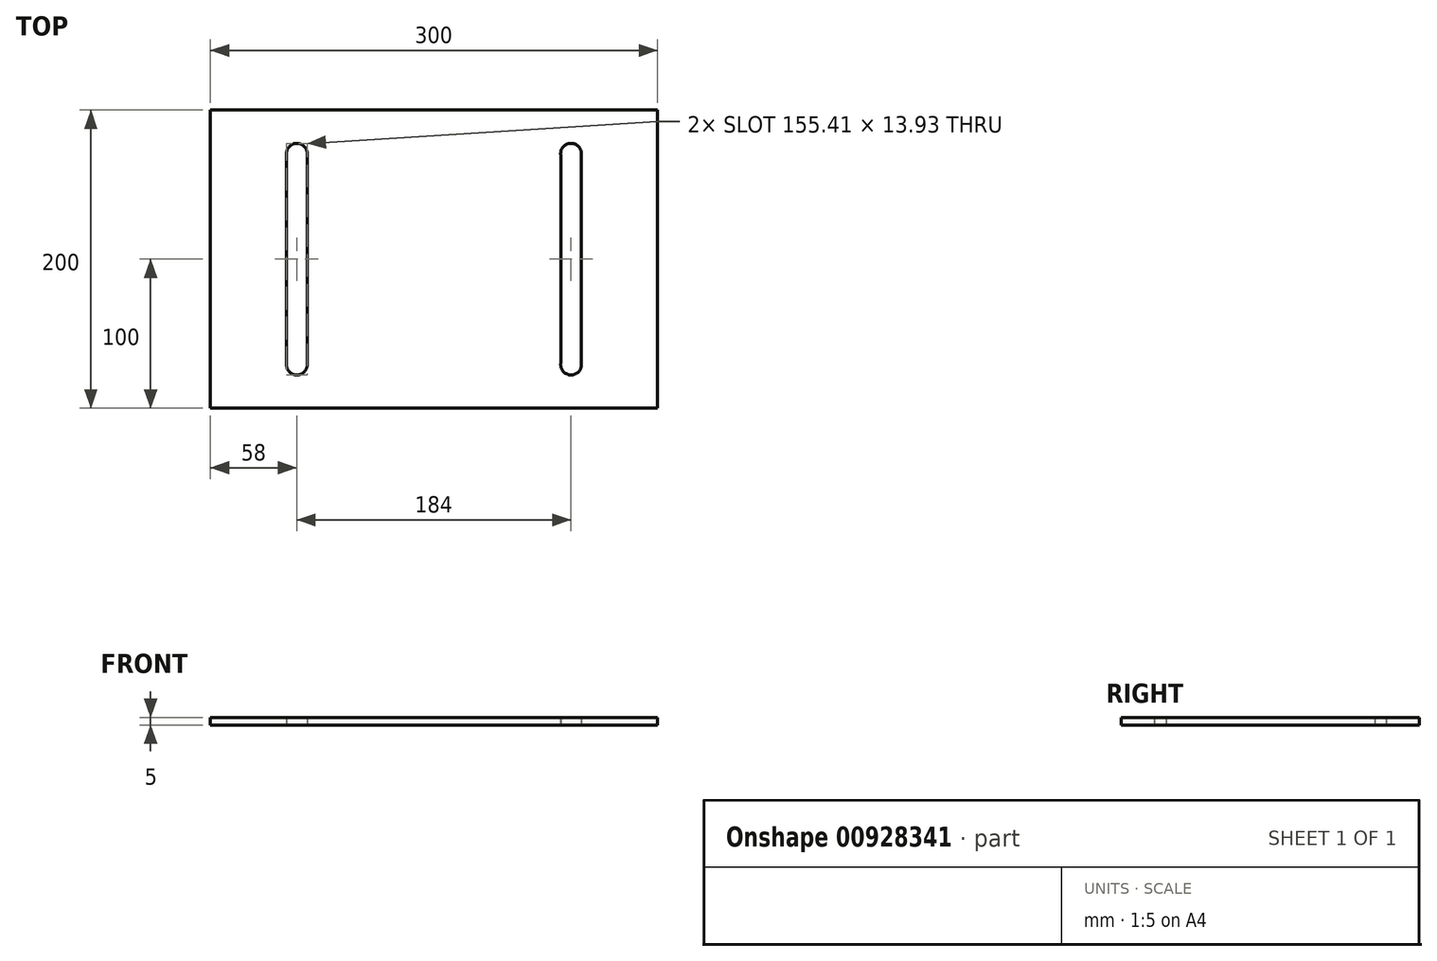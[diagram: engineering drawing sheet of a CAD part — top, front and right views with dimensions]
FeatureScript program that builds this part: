
annotation { "Feature Type Name" : "Feature", "Feature Type Description" : "" }
export const myFeature = defineFeature(function(context is Context, id is Id, definition is map)
    precondition{}
    {
        {
            var Q0;
            Q0=qCreatedBy(makeId("Top.planeOp"),FACE);
            var sketch = newSketch(context, id + "F0", { "sketchPlane" : qUnion([Q0])});
            skLineSegment(sketch, "E0.bottom", {"start": v(150, 100) * mm, "end": v(-150, 100) * mm});
            skLineSegment(sketch, "E0.top", {"start": v(150, -100) * mm, "end": v(-150, -100) * mm});
            skLineSegment(sketch, "E0.left", {"start": v(150, 100) * mm, "end": v(150, -100) * mm});
            skLineSegment(sketch, "E0.right", {"start": v(-150, 100) * mm, "end": v(-150, -100) * mm});
            skPoint(sketch, "E0.middle", {"position": v(0, 0) * mm});
            skLineSegment(sketch, "E1", {"start": v(92, -70) * mm, "end": v(92, 70) * mm, "construction": true});
            skLineSegment(sketch, "E2", {"start": v(85.04, -70) * mm, "end": v(85.04, 70) * mm});
            skLineSegment(sketch, "E3", {"start": v(-150, 0) * mm, "end": v(150, 0) * mm, "construction": true});
            skLineSegment(sketch, "E4", {"start": v(0, 100) * mm, "end": v(0, -100) * mm, "construction": true});
            skArc(sketch, "E5", {"start": v(85.04, -70) * mm, "mid": v(92, -77.7) * mm, "end": v(98.96, -70) * mm});
            skLineSegment(sketch, "E6.MirrorCS", {"start": v(98.96, -70) * mm, "end": v(98.96, 70) * mm});
            skArc(sketch, "E7.MirrorCS", {"start": v(85.04, 70) * mm, "mid": v(92, 77.7) * mm, "end": v(98.96, 70) * mm});
            skLineSegment(sketch, "E8.MirrorCS", {"start": v(-85.04, -70) * mm, "end": v(-85.04, 70) * mm});
            skLineSegment(sketch, "E9.MirrorCS", {"start": v(-98.96, -70) * mm, "end": v(-98.96, 70) * mm});
            skArc(sketch, "E10.MirrorCS", {"start": v(-85.04, 70) * mm, "mid": v(-92, 77.7) * mm, "end": v(-98.96, 70) * mm});
            skArc(sketch, "E11.MirrorCS", {"start": v(-85.04, -70) * mm, "mid": v(-92, -77.7) * mm, "end": v(-98.96, -70) * mm});
            skSolve(sketch);
        }
        {
            var Q0;
            Q0=makeQuery(id+"F0.imprint","IMPRINT",FACE,{"disambiguationData":[TD([[makeQuery(id+"F0.imprint","IMPRINT",EDGE,{"derivedFrom":sQuery(id+"F0.wireOp",EDGE,"E0.bottom")}),1.0]])]});
            extrude(context, id + "F1", {"entities" : qUnion([Q0]), "depth" : 5 * mm, "offsetDistance" : 25 * mm});
        }
    });
